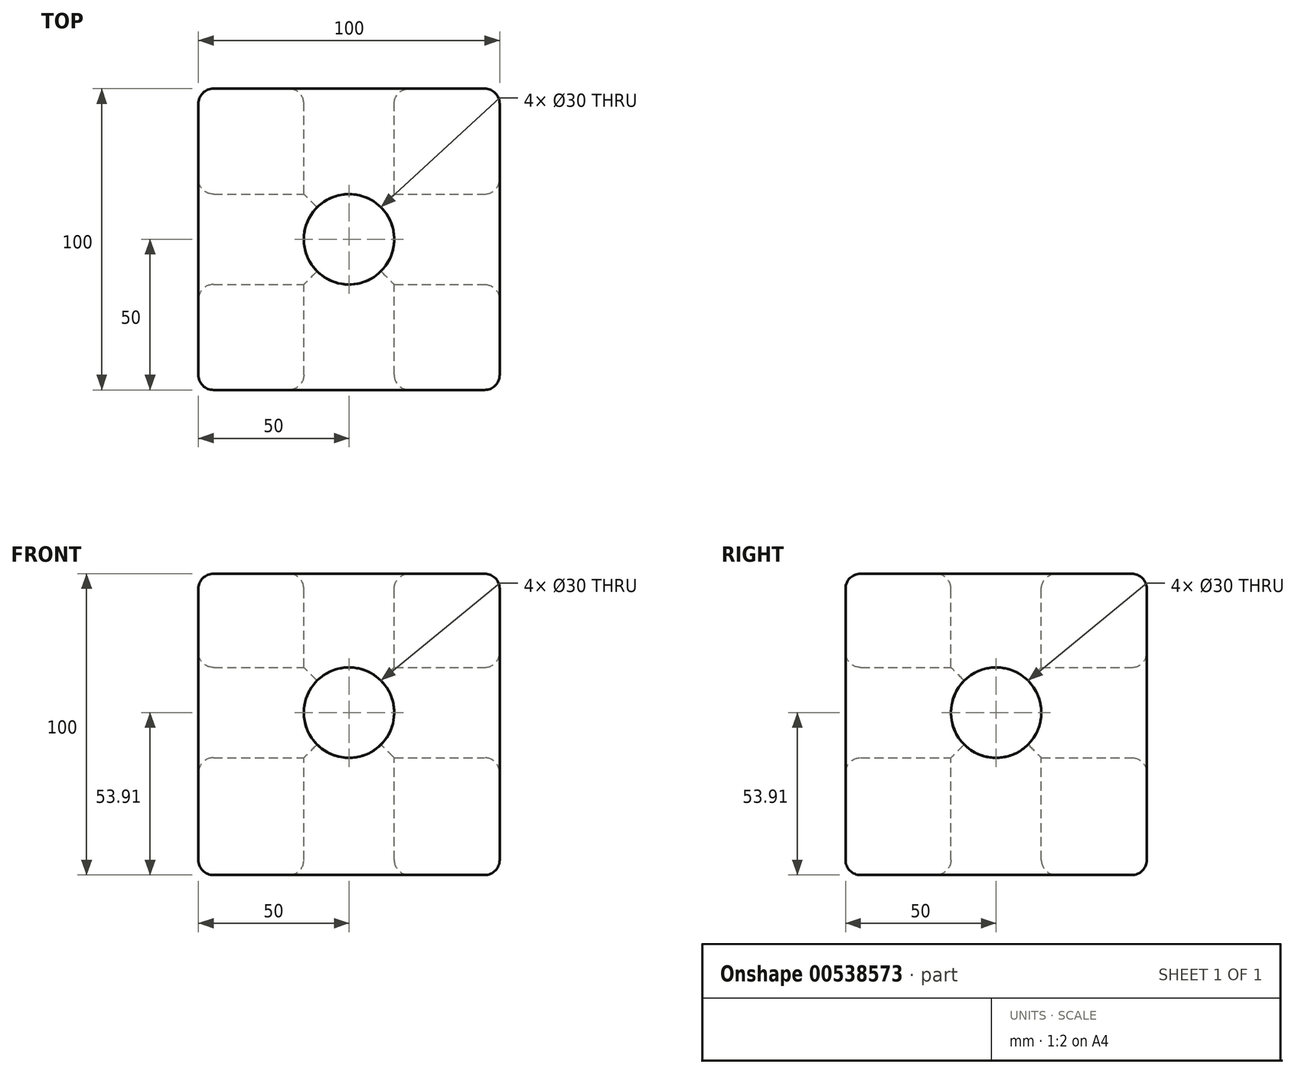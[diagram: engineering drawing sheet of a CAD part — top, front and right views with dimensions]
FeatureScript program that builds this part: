
annotation { "Feature Type Name" : "Feature", "Feature Type Description" : "" }
export const myFeature = defineFeature(function(context is Context, id is Id, definition is map)
    precondition{}
    {
        {
            var Q0;
            Q0=qCreatedBy(makeId("Front.planeOp"),FACE);
            var sketch = newSketch(context, id + "F0", { "sketchPlane" : qUnion([Q0])});
            skLineSegment(sketch, "E0.bottom", {"start": v(50, 46.1) * mm, "end": v(-50, 46.1) * mm});
            skLineSegment(sketch, "E0.top", {"start": v(50, -53.9) * mm, "end": v(-50, -53.9) * mm});
            skLineSegment(sketch, "E0.left", {"start": v(50, 46.1) * mm, "end": v(50, -53.9) * mm});
            skLineSegment(sketch, "E0.right", {"start": v(-50, 46.1) * mm, "end": v(-50, -53.9) * mm});
            skPoint(sketch, "E0.middle", {"position": v(0, -3.9) * mm});
            skCircle(sketch, "E1", {"center": v(0, 0) * mm, "radius": 15 * mm});
            skSolve(sketch);
        }
        {
            var Q0;
            Q0 = qSketchRegion(id + "F0", true);
            extrude(context, id + "F1", {"entities" : qUnion([Q0]), "endBound" : BoundingType.SYMMETRIC, "depth" : 100 * mm, "offsetDistance" : 25 * mm});
        }
        {
            var Q0;
            Q0=makeQuery(id+"F1.opExtrude","SWEPT_FACE",FACE,{"disambiguationData":[OSD([sQuery(id+"F0.wireOp",EDGE,"E0.left")])]});
            var sketch = newSketch(context, id + "F2", { "sketchPlane" : qUnion([Q0])});
            skCircle(sketch, "E2", {"center": v(0, 0) * mm, "radius": 15 * mm});
            skSolve(sketch);
        }
        {
            var Q0;
            Q0=makeQuery(id+"F2.imprint","IMPRINT",FACE,{"disambiguationData":[TD([[makeQuery(id+"F2.imprint","IMPRINT",EDGE,{"derivedFrom":sQuery(id+"F2.wireOp",EDGE,"E2")}),1.0]])]});
            extrude(context, id + "F3", {"entities" : qUnion([Q0]), "operationType" : NewBodyOperationType.REMOVE, "oppositeDirection" : true, "depth" : 100 * mm, "offsetDistance" : 25 * mm});
        }
        {
            var Q0;
            Q0=makeQuery(id+"F1.opExtrude","SWEPT_FACE",FACE,{"disambiguationData":[OSD([sQuery(id+"F0.wireOp",EDGE,"E0.bottom")])]});
            var sketch = newSketch(context, id + "F4", { "sketchPlane" : qUnion([Q0])});
            skCircle(sketch, "E3", {"center": v(0, 0) * mm, "radius": 15 * mm});
            skSolve(sketch);
        }
        {
            var Q0;
            Q0=makeQuery(id+"F4.imprint","IMPRINT",FACE,{"disambiguationData":[TD([[makeQuery(id+"F4.imprint","IMPRINT",EDGE,{"derivedFrom":sQuery(id+"F4.wireOp",EDGE,"E3")}),1.0]])]});
            extrude(context, id + "F5", {"entities" : qUnion([Q0]), "operationType" : NewBodyOperationType.REMOVE, "oppositeDirection" : true, "depth" : 100 * mm, "offsetDistance" : 25 * mm});
        }
        {
            var Q0;
            Q0=makeQuery(id+"F1.opExtrude","SWEPT_FACE",FACE,{"disambiguationData":[OSD([sQuery(id+"F0.wireOp",EDGE,"E0.top")])]});
            var Q1;
            Q1=makeQuery(id+"F1.opExtrude","CAP_FACE",FACE,{"disambiguationData":[OSD([sQuery(id+"F0.wireOp",EDGE,"E0.bottom"),sQuery(id+"F0.wireOp",EDGE,"E0.top"),sQuery(id+"F0.wireOp",EDGE,"E0.left"),sQuery(id+"F0.wireOp",EDGE,"E0.right"),sQuery(id+"F0.wireOp",EDGE,"E1")])],"isStart":false});
            var Q2;
            Q2=makeQuery(id+"F1.opExtrude","SWEPT_FACE",FACE,{"disambiguationData":[OSD([sQuery(id+"F0.wireOp",EDGE,"E0.left")])]});
            var Q3;
            Q3=makeQuery(id+"F1.opExtrude","SWEPT_FACE",FACE,{"disambiguationData":[OSD([sQuery(id+"F0.wireOp",EDGE,"E0.bottom")])]});
            var Q4;
            Q4=makeQuery(id+"F1.opExtrude","CAP_FACE",FACE,{"disambiguationData":[OSD([sQuery(id+"F0.wireOp",EDGE,"E0.bottom"),sQuery(id+"F0.wireOp",EDGE,"E0.top"),sQuery(id+"F0.wireOp",EDGE,"E0.left"),sQuery(id+"F0.wireOp",EDGE,"E0.right"),sQuery(id+"F0.wireOp",EDGE,"E1")])],"isStart":true});
            var Q5;
            Q5=makeQuery(id+"F1.opExtrude","SWEPT_FACE",FACE,{"disambiguationData":[OSD([sQuery(id+"F0.wireOp",EDGE,"E0.right")])]});
            fillet(context, id + "F6", {"entities" : qUnion([Q0, Q1, Q2, Q3, Q4, Q5]), "radius" : 5 * mm, "tangentPropagation" : true, "allowEdgeOverflow" : false});
        }
    });
